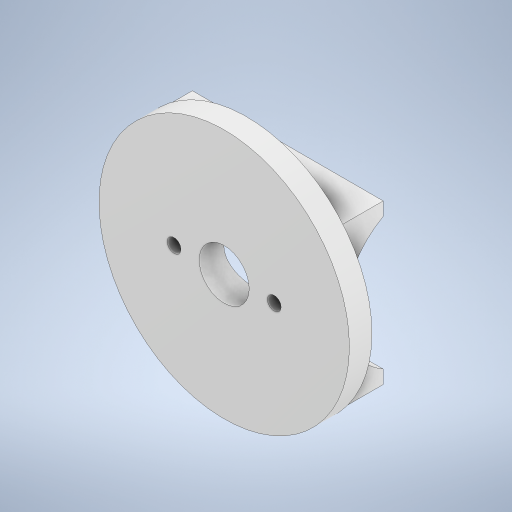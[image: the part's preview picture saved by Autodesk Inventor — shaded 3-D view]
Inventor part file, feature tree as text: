
AUTODESK INVENTOR PART (.ipt)
format: ipt  version: 2023 (Build 270158030, 158C)  size: 267,264 bytes
history: native  units: in
note: dims shown in document units (in); Inventor stores cm internally (conversion verified against a paired STEP export)
features: sketch x4, extrude x3, hole x1
ambient origin geometry x8: Origin, YZ Plane, XZ Plane, XY Plane, X Axis, Y Axis, Z Axis, Center Point
bodies: Solid1 (feature_tree)
feature tree (8):
  extrude  "Extrusion1"  Depth=2.5in
  extrude  "Extrusion2"  Depth=1.0in
  extrude  "Extrusion3"  Depth=3.937in
  hole  "Hole1"  [1 undecoded]
  sketch  "Sketch1"  dims[d1=2.375in d3=2.5in]
  sketch  "Sketch2"  dims[d4=1.5748in d5=1.0in]
  sketch  "Sketch3"  dims[d6=3.0in d7=0.0in d8=3.937in]
  sketch  "Sketch5"  dims[d9=0.3543in d10=0.0in d11=0.7874in d12=0.0in d13=0.0in d14=0.2165in d15=0.3389in d16=0.0246in d17=0.426in d18=0.5906in d19=0.1693in d20=90.0deg d21=0.3543in d22=0.8108in d23=1.5748in d24=0.0394in d25=0.0394in d26=0.0394in d27=0.0059in d28=0.0098in d29=0.0148in d30=0.5635in d31=0.0295in d32=0.8108in d33=0.0025in d34=0.0295in d35=0.0148in]
note: 1 required parameter value undecoded (feature->parameter linkage not recoverable at this tier; creation-order binding heuristic only, values carry confidence <= 0.55)
